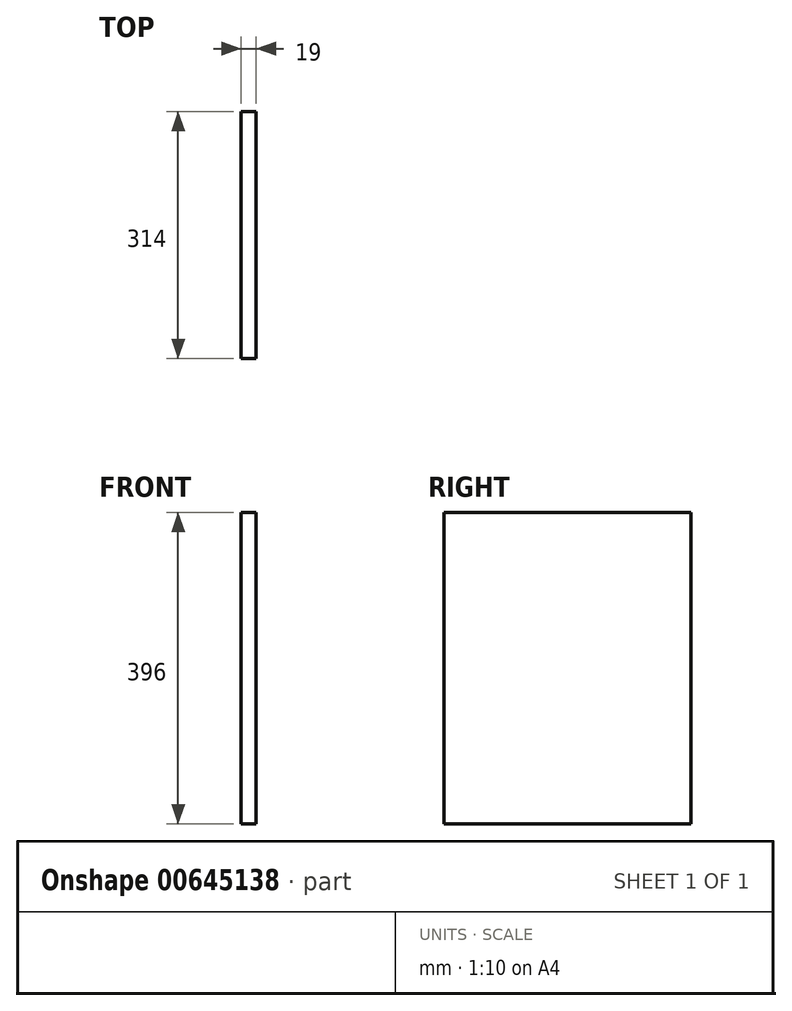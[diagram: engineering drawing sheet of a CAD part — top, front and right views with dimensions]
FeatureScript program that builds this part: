
annotation { "Feature Type Name" : "Feature", "Feature Type Description" : "" }
export const myFeature = defineFeature(function(context is Context, id is Id, definition is map)
    precondition{}
    {
        {
            var Q0;
            Q0=qCreatedBy(makeId("Right.planeOp"),FACE);
            var sketch = newSketch(context, id + "F0", { "sketchPlane" : qUnion([Q0])});
            skLineSegment(sketch, "E0.bottom", {"start": v(157, -198) * mm, "end": v(-157, -198) * mm});
            skLineSegment(sketch, "E0.top", {"start": v(157, 198) * mm, "end": v(-157, 198) * mm});
            skLineSegment(sketch, "E0.left", {"start": v(157, -198) * mm, "end": v(157, 198) * mm});
            skLineSegment(sketch, "E0.right", {"start": v(-157, -198) * mm, "end": v(-157, 198) * mm});
            skPoint(sketch, "E0.middle", {"position": v(0, 0) * mm});
            skSolve(sketch);
        }
        {
            var Q0;
            Q0 = qSketchRegion(id + "F0", true);
            extrude(context, id + "F1", {"entities" : qUnion([Q0]), "depth" : 19 * mm, "offsetDistance" : 25.4 * mm});
        }
    });
